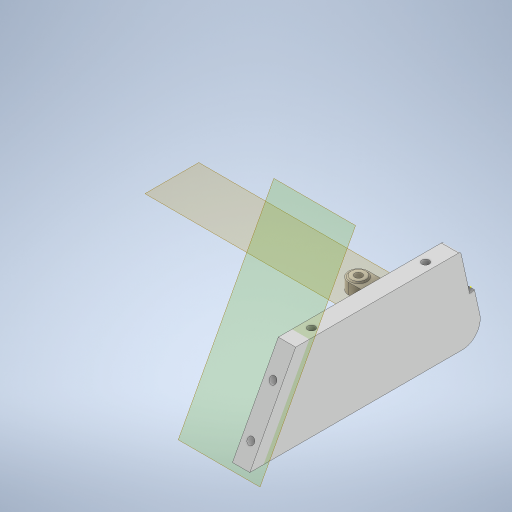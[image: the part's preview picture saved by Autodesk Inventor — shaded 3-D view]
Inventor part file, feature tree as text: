
AUTODESK INVENTOR PART (.ipt)
format: ipt  version: 2023 (Build 270158000, 158)  size: 650,240 bytes
history: native  units: in
note: dims shown in document units (in); Inventor stores cm internally (conversion verified against a paired STEP export)
features: sketch x31, other x8, extrude x2, projected_geometry x2
ambient origin geometry x8: Origin, YZ Plane, XZ Plane, XY Plane, X Axis, Y Axis, Z Axis, Center Point
bodies: Body1 (feature_tree)
feature tree (43):
  other  "sciana_awaryjna.ipt"
  extrude  "Wyciągnięcie proste1"  Depth=0.3937in
  extrude  "Wyciągnięcie proste2"  Depth=0.3937in TaperAngle=0.0deg
  other  "Bryła1::sciana_awaryjna.ipt"
  other  "Bryła wyprowadzona1"
  sketch  "Szkic1"
  sketch  "Szkic2"
  sketch  "Szkic3"
  sketch  "Szkic4"
  sketch  "Szkic5"
  sketch  "Szkic6"
  sketch  "Szkic7"
  sketch  "Szkic8"
  sketch  "Szkic9"
  sketch  "Szkic12"
  sketch  "Szkic13"
  sketch  "Szkic14"
  sketch  "Szkic15"
  sketch  "Szkic16"
  sketch  "Szkic17"
  sketch  "Szkic18"
  sketch  "Szkic19"
  sketch  "Szkic20"
  sketch  "Szkic21"
  sketch  "Szkic22"
  sketch  "Szkic23"
  sketch  "Szkic24"
  sketch  "Szkic25"
  sketch  "Szkic26"
  sketch  "Szkic27"
  sketch  "Szkic28"
  sketch  "Szkic29"
  sketch  "Szkic30"
  sketch  "Szkic31"
  other  "Płaszczyzna konstrukcyjna1"
  other  "Płaszczyzna konstrukcyjna2"
  other  "Płaszczyzna konstrukcyjna3"
  other  "Płaszczyzna konstrukcyjna4"
  sketch  "Szkic32"
  projected_geometry  "Pętla rzutowana1"
  sketch  "Szkic33"
  projected_geometry  "Pętla rzutowana2"
  other  "Bryła1"
